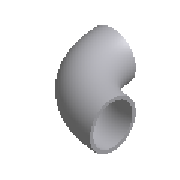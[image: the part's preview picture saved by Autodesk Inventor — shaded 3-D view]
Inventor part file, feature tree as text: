
AUTODESK INVENTOR PART (.ipt)
format: ipt  version: 2023.1 (Build 271208000, 208)  size: 183,808 bytes
history: native  units: mm (DEFAULTED — no unit token found)
features: other x4, sketch x2, sweep x1
ambient origin geometry x8: Origin, YZ Plane, XZ Plane, XY Plane, X Axis, Y Axis, Z Axis, Center Point
bodies: Solid1 (feature_tree)
feature tree (7):
  sweep  "Sweep1"
  other  "Work Point1"
  other  "Work Point2"
  other  "Work Axis1"
  other  "Work Axis2"
  sketch  "Sketch1"  dims[d0=56.3mm d1=60.3mm]
  sketch  "Sketch2"  dims[d2=76.0mm d3=76.0mm d4=0.0mm d5=0.0mm]
